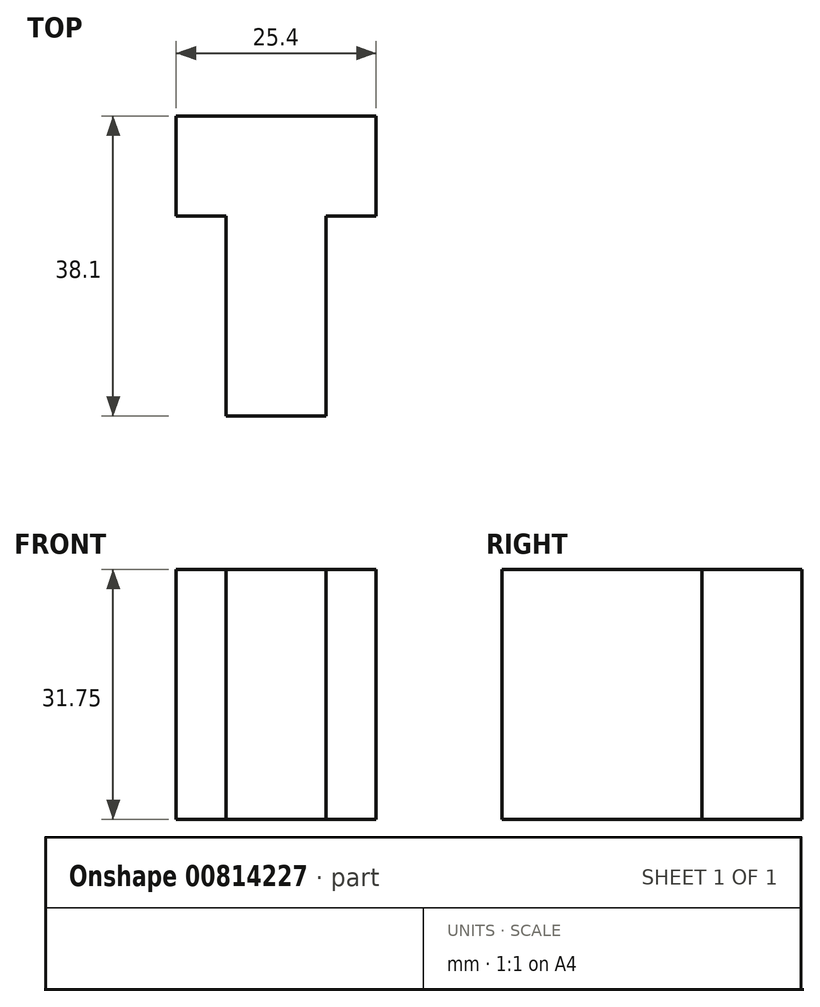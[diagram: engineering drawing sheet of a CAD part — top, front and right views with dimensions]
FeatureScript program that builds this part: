
annotation { "Feature Type Name" : "Feature", "Feature Type Description" : "" }
export const myFeature = defineFeature(function(context is Context, id is Id, definition is map)
    precondition{}
    {
        {
            var Q0;
            Q0=qCreatedBy(makeId("Top.planeOp"),FACE);
            var sketch = newSketch(context, id + "F0", { "sketchPlane" : qUnion([Q0])});
            skLineSegment(sketch, "E0", {"start": v(0, 45.42) * mm, "end": v(25.4, 45.42) * mm});
            skLineSegment(sketch, "E1", {"start": v(25.4, 45.42) * mm, "end": v(25.4, 32.72) * mm});
            skLineSegment(sketch, "E2", {"start": v(0, 45.42) * mm, "end": v(0, 32.72) * mm});
            skLineSegment(sketch, "E3", {"start": v(0, 32.72) * mm, "end": v(6.35, 32.72) * mm});
            skLineSegment(sketch, "E4", {"start": v(25.4, 32.72) * mm, "end": v(19.05, 32.72) * mm});
            skLineSegment(sketch, "E5", {"start": v(6.35, 32.72) * mm, "end": v(6.35, 7.32) * mm});
            skLineSegment(sketch, "E6", {"start": v(19.05, 32.72) * mm, "end": v(19.05, 7.32) * mm});
            skLineSegment(sketch, "E7", {"start": v(6.35, 7.32) * mm, "end": v(19.05, 7.32) * mm});
            skSolve(sketch);
        }
        {
            var Q0;
            Q0=makeQuery(id+"F0.imprint","IMPRINT",FACE,{"disambiguationData":[TD([[makeQuery(id+"F0.imprint","IMPRINT",EDGE,{"derivedFrom":sQuery(id+"F0.wireOp",EDGE,"E0")}),-1.0]])]});
            extrude(context, id + "F1", {"entities" : qUnion([Q0]), "depth" : 31.75 * mm, "offsetDistance" : 25.4 * mm});
        }
    });
